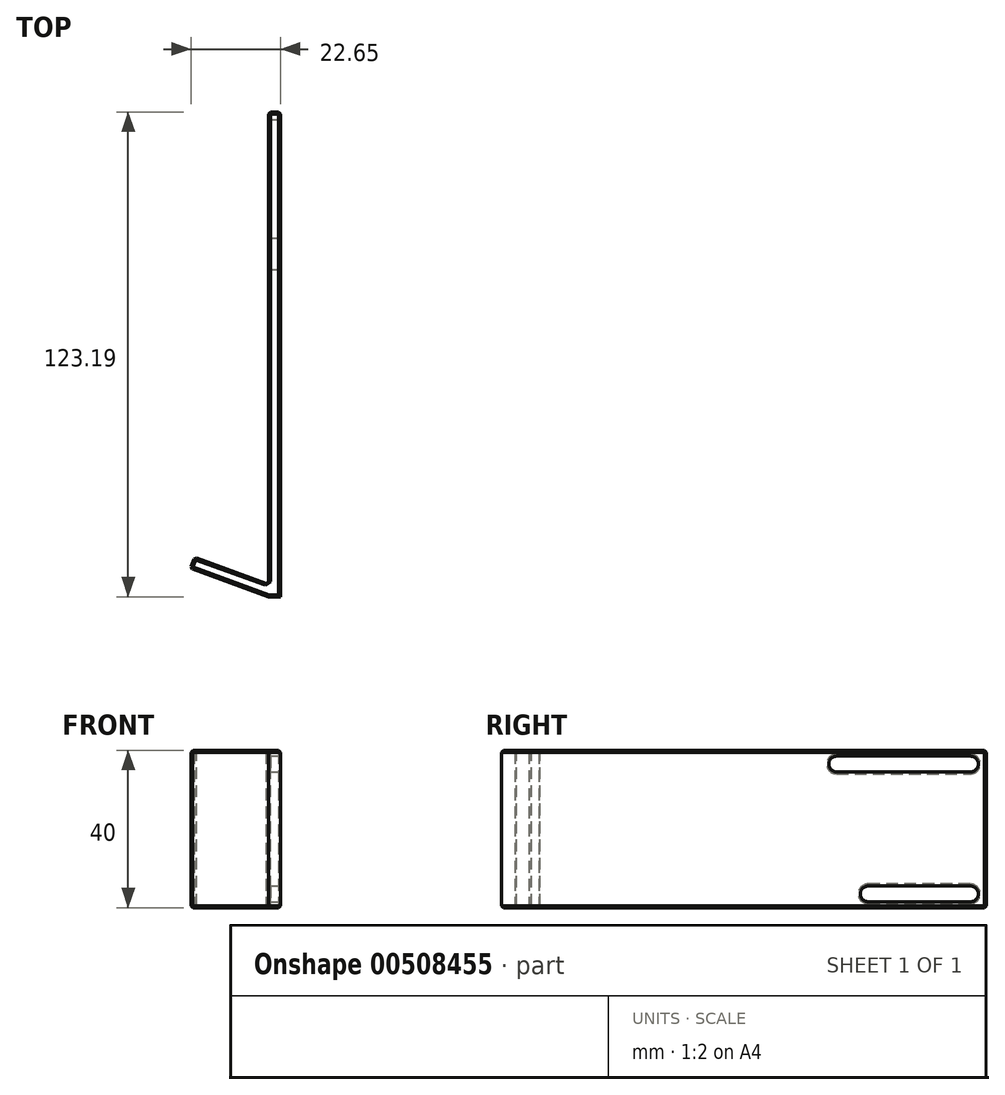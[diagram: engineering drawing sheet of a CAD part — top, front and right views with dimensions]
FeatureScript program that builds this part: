
annotation { "Feature Type Name" : "Feature", "Feature Type Description" : "" }
export const myFeature = defineFeature(function(context is Context, id is Id, definition is map)
    precondition{}
    {
        {
            var Q0;
            Q0=qCreatedBy(makeId("Top.planeOp"),FACE);
            var sketch = newSketch(context, id + "F0", { "sketchPlane" : qUnion([Q0])});
            skLineSegment(sketch, "E0.bottom", {"start": v(0, 60) * mm, "end": v(3, 60) * mm});
            skLineSegment(sketch, "E0.top", {"start": v(0, -60) * mm, "end": v(3, -60) * mm});
            skLineSegment(sketch, "E0.left", {"start": v(0, 60) * mm, "end": v(0, -60) * mm});
            skLineSegment(sketch, "E0.right", {"start": v(3, 60) * mm, "end": v(3, -60) * mm});
            skLineSegment(sketch, "E1", {"start": v(0, -60) * mm, "end": v(-18.8, -53.16) * mm});
            skLineSegment(sketch, "E2", {"start": v(-18.8, -53.16) * mm, "end": v(-19.82, -55.98) * mm});
            skLineSegment(sketch, "E3", {"start": v(-19.82, -55.98) * mm, "end": v(0, -63.2) * mm});
            skLineSegment(sketch, "E4", {"start": v(0, -63.2) * mm, "end": v(3, -63.2) * mm});
            skLineSegment(sketch, "E5", {"start": v(3, -63.2) * mm, "end": v(3, -60) * mm});
            skSolve(sketch);
        }
        {
            var Q0;
            Q0 = qSketchRegion(id + "F0", true);
            extrude(context, id + "F1", {"entities" : qUnion([Q0]), "depth" : 40 * mm, "offsetDistance" : 25 * mm});
        }
        {
            var Q0;
            Q0=makeQuery(id+"F1.opExtrude","SWEPT_FACE",FACE,{"disambiguationData":[OSD([sQuery(id+"F0.wireOp",EDGE,"E0.right"),sQuery(id+"F0.wireOp",EDGE,"E5")])]});
            var sketch = newSketch(context, id + "F2", { "sketchPlane" : qUnion([Q0])});
            skLineSegment(sketch, "E6.bottom", {"start": v(56, 38.5) * mm, "end": v(22, 38.5) * mm});
            skLineSegment(sketch, "E6.top", {"start": v(56, 34.5) * mm, "end": v(22, 34.5) * mm});
            skLineSegment(sketch, "E6.left", {"start": v(56, 38.5) * mm, "end": v(56, 34.5) * mm});
            skLineSegment(sketch, "E6.right", {"start": v(22, 38.5) * mm, "end": v(22, 34.5) * mm});
            skCircle(sketch, "E7", {"center": v(56, 36.5) * mm, "radius": 2 * mm});
            skCircle(sketch, "E8", {"center": v(22, 36.5) * mm, "radius": 2 * mm});
            skLineSegment(sketch, "E9.bottom", {"start": v(30, 5.5) * mm, "end": v(56, 5.5) * mm});
            skLineSegment(sketch, "E9.top", {"start": v(30, 1.5) * mm, "end": v(56, 1.5) * mm});
            skLineSegment(sketch, "E9.left", {"start": v(30, 5.5) * mm, "end": v(30, 1.5) * mm});
            skLineSegment(sketch, "E9.right", {"start": v(56, 5.5) * mm, "end": v(56, 1.5) * mm});
            skCircle(sketch, "E10", {"center": v(30, 3.5) * mm, "radius": 2 * mm});
            skCircle(sketch, "E11", {"center": v(56, 3.5) * mm, "radius": 2 * mm});
            skSolve(sketch);
        }
        {
            var Q0;
            {var subQ0=sQuery(id+"F2.wireOp",EDGE,"E6.bottom");Q0=makeQuery(id+"F2.imprint","IMPRINT",FACE,{"disambiguationData":[TD([[makeQuery(id+"F2.imprint","IMPRINT",EDGE,{"derivedFrom":subQ0}),1.0]])]});}
            var Q1;
            {var subQ0=sQuery(id+"F2.wireOp",EDGE,"E6.left");Q1=makeQuery(id+"F2.imprint","IMPRINT",FACE,{"disambiguationData":[TD([[makeQuery(id+"F2.imprint","IMPRINT",EDGE,{"derivedFrom":subQ0}),-1.0]])]});}
            var Q2;
            {var subQ0=sQuery(id+"F2.wireOp",EDGE,"E6.left");Q2=makeQuery(id+"F2.imprint","IMPRINT",FACE,{"disambiguationData":[TD([[makeQuery(id+"F2.imprint","IMPRINT",EDGE,{"derivedFrom":subQ0}),1.0]])]});}
            var Q3;
            {var subQ0=sQuery(id+"F2.wireOp",EDGE,"E6.right");Q3=makeQuery(id+"F2.imprint","IMPRINT",FACE,{"disambiguationData":[TD([[makeQuery(id+"F2.imprint","IMPRINT",EDGE,{"derivedFrom":subQ0}),1.0]])]});}
            var Q4;
            {var subQ0=sQuery(id+"F2.wireOp",EDGE,"E6.right");Q4=makeQuery(id+"F2.imprint","IMPRINT",FACE,{"disambiguationData":[TD([[makeQuery(id+"F2.imprint","IMPRINT",EDGE,{"derivedFrom":subQ0}),-1.0]])]});}
            var Q5;
            {var subQ0=sQuery(id+"F2.wireOp",EDGE,"E9.bottom");Q5=makeQuery(id+"F2.imprint","IMPRINT",FACE,{"disambiguationData":[TD([[makeQuery(id+"F2.imprint","IMPRINT",EDGE,{"derivedFrom":subQ0}),-1.0]])]});}
            var Q6;
            {var subQ0=sQuery(id+"F2.wireOp",EDGE,"E9.left");Q6=makeQuery(id+"F2.imprint","IMPRINT",FACE,{"disambiguationData":[TD([[makeQuery(id+"F2.imprint","IMPRINT",EDGE,{"derivedFrom":subQ0}),1.0]])]});}
            var Q7;
            {var subQ0=sQuery(id+"F2.wireOp",EDGE,"E9.left");Q7=makeQuery(id+"F2.imprint","IMPRINT",FACE,{"disambiguationData":[TD([[makeQuery(id+"F2.imprint","IMPRINT",EDGE,{"derivedFrom":subQ0}),-1.0]])]});}
            var Q8;
            {var subQ0=sQuery(id+"F2.wireOp",EDGE,"E9.right");Q8=makeQuery(id+"F2.imprint","IMPRINT",FACE,{"disambiguationData":[TD([[makeQuery(id+"F2.imprint","IMPRINT",EDGE,{"derivedFrom":subQ0}),-1.0]])]});}
            var Q9;
            {var subQ0=sQuery(id+"F2.wireOp",EDGE,"E9.right");Q9=makeQuery(id+"F2.imprint","IMPRINT",FACE,{"disambiguationData":[TD([[makeQuery(id+"F2.imprint","IMPRINT",EDGE,{"derivedFrom":subQ0}),1.0]])]});}
            extrude(context, id + "F3", {"entities" : qUnion([Q0, Q1, Q2, Q3, Q4, Q5, Q6, Q7, Q8, Q9]), "operationType" : NewBodyOperationType.REMOVE, "oppositeDirection" : true, "depth" : 25 * mm, "offsetDistance" : 25 * mm});
        }
        {
            var Q0;
            Q0=makeQuery(id+"F1.opExtrude","CAP_FACE",FACE,{"disambiguationData":[OSD([sQuery(id+"F0.wireOp",EDGE,"E0.bottom"),sQuery(id+"F0.wireOp",EDGE,"E0.left"),sQuery(id+"F0.wireOp",EDGE,"E0.right"),sQuery(id+"F0.wireOp",EDGE,"E1"),sQuery(id+"F0.wireOp",EDGE,"E2"),sQuery(id+"F0.wireOp",EDGE,"E3"),sQuery(id+"F0.wireOp",EDGE,"E4"),sQuery(id+"F0.wireOp",EDGE,"E5")])],"isStart":false});
            var Q1;
            Q1=makeQuery(id+"F1.opExtrude","SWEPT_FACE",FACE,{"disambiguationData":[OSD([sQuery(id+"F0.wireOp",EDGE,"E0.bottom")])]});
            var Q2;
            Q2=makeQuery(id+"F1.opExtrude","CAP_FACE",FACE,{"disambiguationData":[OSD([sQuery(id+"F0.wireOp",EDGE,"E0.bottom"),sQuery(id+"F0.wireOp",EDGE,"E0.left"),sQuery(id+"F0.wireOp",EDGE,"E0.right"),sQuery(id+"F0.wireOp",EDGE,"E1"),sQuery(id+"F0.wireOp",EDGE,"E2"),sQuery(id+"F0.wireOp",EDGE,"E3"),sQuery(id+"F0.wireOp",EDGE,"E4"),sQuery(id+"F0.wireOp",EDGE,"E5")])],"isStart":true});
            var Q3;
            Q3=makeQuery(id+"F1.opExtrude","SWEPT_FACE",FACE,{"disambiguationData":[OSD([sQuery(id+"F0.wireOp",EDGE,"E2")])]});
            var Q4;
            Q4=makeQuery(id+"F3.boolean.opBoolean","INTERSECT",EDGE,{"derivedFrom":[makeQuery(id+"F1.opExtrude","SWEPT_FACE",FACE,{"disambiguationData":[OSD([sQuery(id+"F0.wireOp",EDGE,"E0.left")])]}),makeQuery(id+"F3.opExtrude","SWEPT_FACE",FACE,{"disambiguationData":[OSD([sQuery(id+"F2.wireOp",EDGE,"E8")])]})]});
            var Q5;
            Q5=makeQuery(id+"F1.opExtrude","SWEPT_FACE",FACE,{"disambiguationData":[OSD([sQuery(id+"F0.wireOp",EDGE,"E0.left")])]});
            var Q6;
            Q6=makeQuery(id+"F3.boolean.opBoolean","COPY",EDGE,{"derivedFrom":makeQuery(id+"F3.opExtrude","CAP_EDGE",EDGE,{"disambiguationData":[OSD([sQuery(id+"F2.wireOp",EDGE,"E9.bottom")])],"isStart":true})});
            var Q7;
            Q7=makeQuery(id+"F3.boolean.opBoolean","COPY",EDGE,{"derivedFrom":makeQuery(id+"F3.opExtrude","CAP_EDGE",EDGE,{"disambiguationData":[OSD([sQuery(id+"F2.wireOp",EDGE,"E6.top")])],"isStart":true})});
            chamfer(context, id + "F4", {"entities" : qUnion([Q0, Q1, Q2, Q3, Q4, Q5, Q6, Q7]), "width" : .5 * mm, "tangentPropagation" : true});
        }
    });
